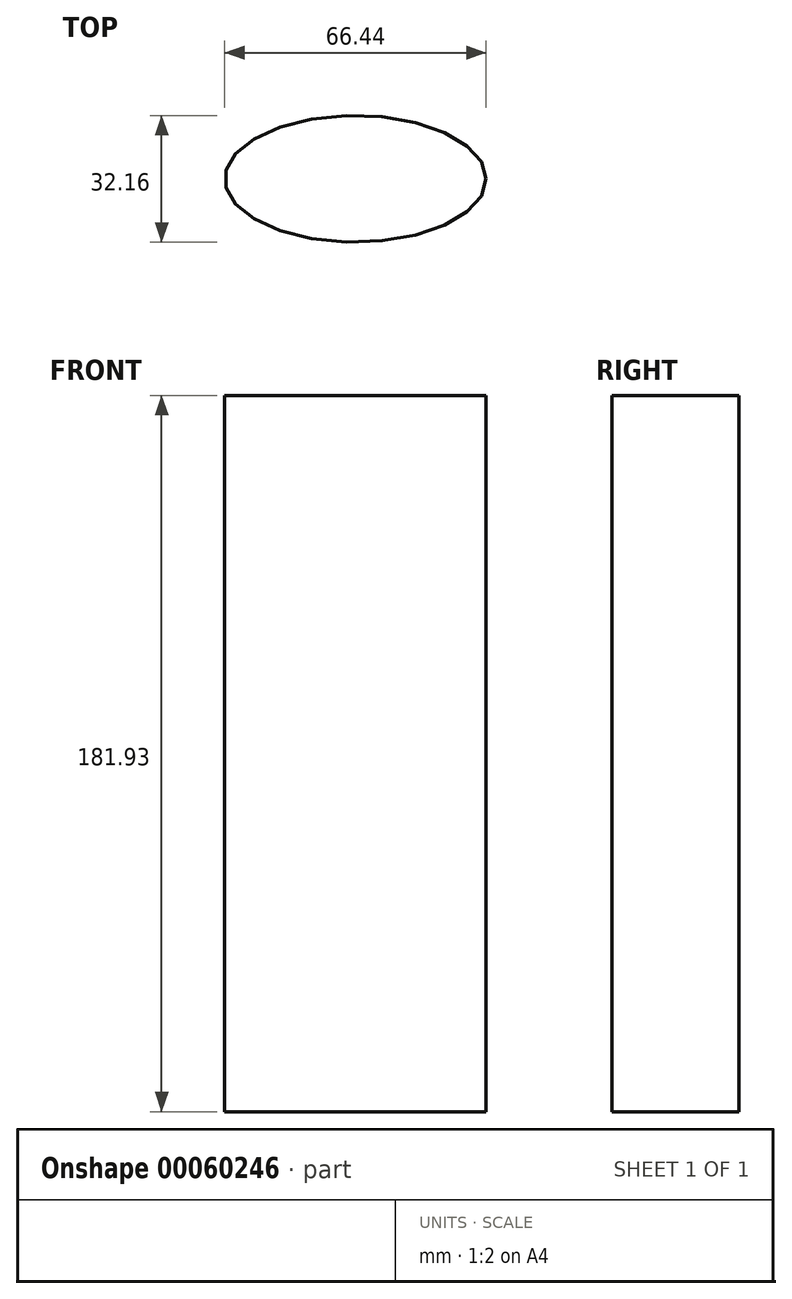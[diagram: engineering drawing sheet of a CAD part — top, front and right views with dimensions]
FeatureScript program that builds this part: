
annotation { "Feature Type Name" : "Feature", "Feature Type Description" : "" }
export const myFeature = defineFeature(function(context is Context, id is Id, definition is map)
    precondition{}
    {
        {
            var Q0;
            Q0=qCreatedBy(makeId("Top.planeOp"),FACE);
            var sketch = newSketch(context, id + "F0", { "sketchPlane" : qUnion([Q0])});
            skEllipse(sketch, "E0", {"center": v(0, 0) * mm, "majorRadius": 33.22 * mm, "minorRadius": 16.08 * mm, "majorAxis": v(1, 0)});
            skSolve(sketch);
        }
        {
            var Q0;
            Q0=makeQuery(id+"F0.imprint","IMPRINT",FACE,{"disambiguationData":[TD([[makeQuery(id+"F0.imprint","IMPRINT",EDGE,{"derivedFrom":sQuery(id+"F0.wireOp",EDGE,"E0")}),1.0]])]});
            extrude(context, id + "F1", {"entities" : qUnion([Q0]), "depth" : 112.63 * mm, "hasSecondDirection" : true, "secondDirectionOppositeDirection" : true, "secondDirectionDepth" : 69.3 * mm});
        }
        {
            var Q0;
            Q0=qCreatedBy(makeId("Right.planeOp"),FACE);
            var sketch = newSketch(context, id + "F2", { "sketchPlane" : qUnion([Q0])});
            skCircle(sketch, "E1", {"center": v(-20.4, 80.49) * mm, "radius": 10.08 * mm});
            skCircle(sketch, "E2", {"center": v(-20.4, 59.73) * mm, "radius": 10.08 * mm});
            skCircle(sketch, "E3", {"center": v(-20.76, 38.97) * mm, "radius": 10.08 * mm});
            skSolve(sketch);
        }
        {
            var Q0;
            Q0=sQuery(id+"F2.wireOp",EDGE,"E3");
            var Q1;
            Q1=sQuery(id+"F2.wireOp",EDGE,"E2");
            var Q2;
            Q2=sQuery(id+"F2.wireOp",EDGE,"E1");
            extrude(context, id + "F3", {"bodyType" : ToolBodyType.SURFACE, "surfaceEntities" : qUnion([Q0, Q1, Q2]), "depth" : 75.3 * mm, "hasSecondDirection" : true, "secondDirectionOppositeDirection" : true, "secondDirectionDepth" : 79.28 * mm});
        }
    });
